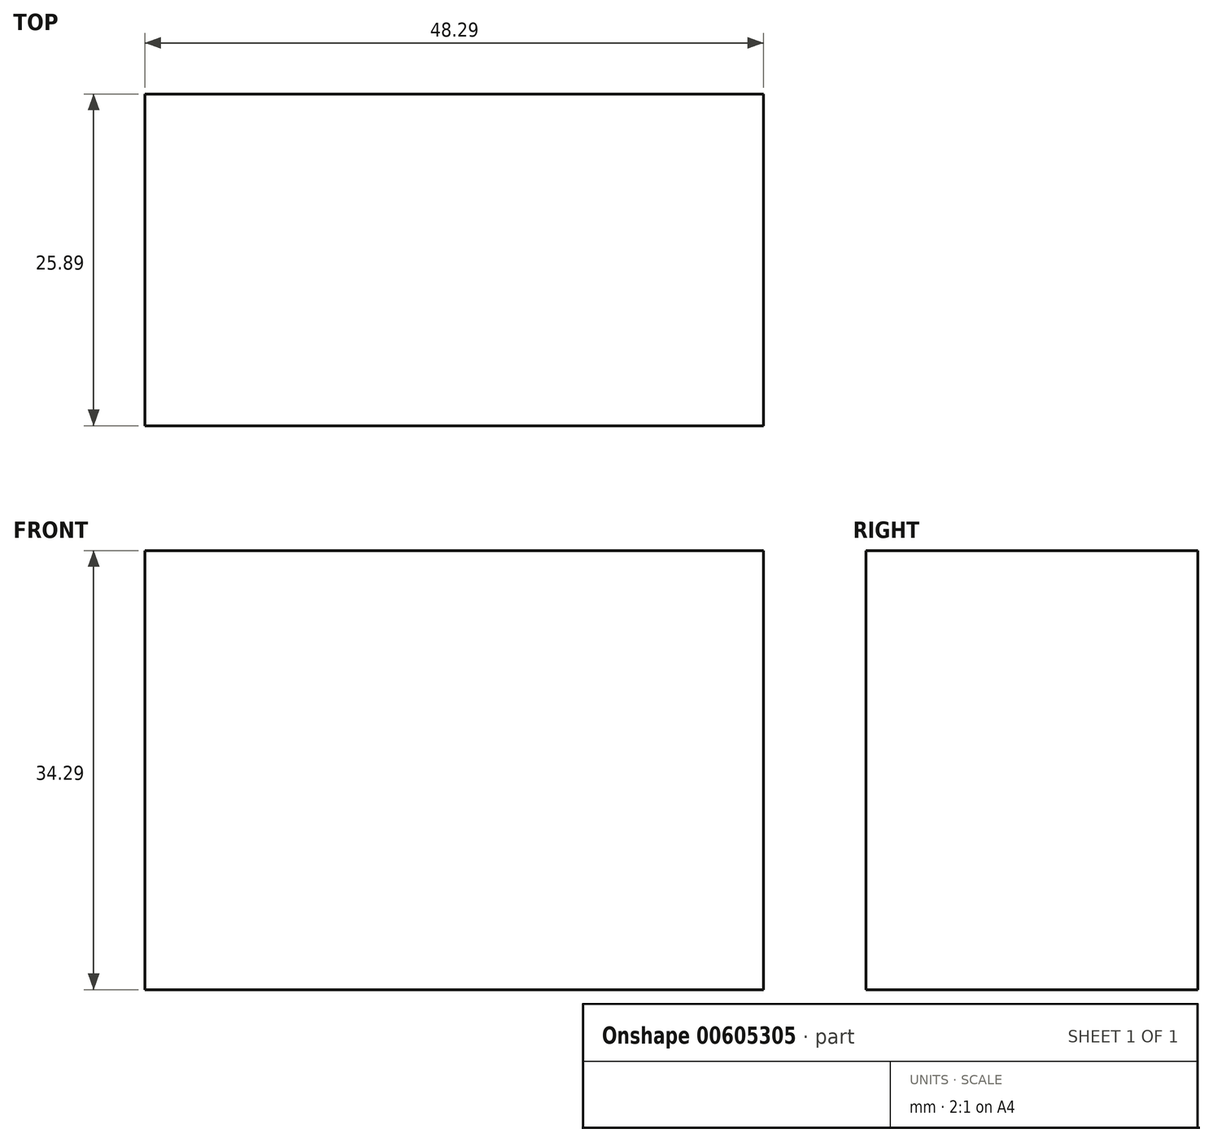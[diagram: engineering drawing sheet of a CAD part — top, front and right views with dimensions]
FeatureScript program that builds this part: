
annotation { "Feature Type Name" : "Feature", "Feature Type Description" : "" }
export const myFeature = defineFeature(function(context is Context, id is Id, definition is map)
    precondition{}
    {
        {
            var Q0;
            Q0=qCreatedBy(makeId("Top.planeOp"),FACE);
            var sketch = newSketch(context, id + "F0", { "sketchPlane" : qUnion([Q0])});
            skLineSegment(sketch, "E0.bottom", {"start": v(0, 0) * mm, "end": v(48.29, 0) * mm});
            skLineSegment(sketch, "E0.top", {"start": v(0, 25.9) * mm, "end": v(48.29, 25.9) * mm});
            skLineSegment(sketch, "E0.left", {"start": v(0, 0) * mm, "end": v(0, 25.9) * mm});
            skLineSegment(sketch, "E0.right", {"start": v(48.29, 0) * mm, "end": v(48.29, 25.9) * mm});
            skSolve(sketch);
        }
        {
            var Q0;
            Q0 = qSketchRegion(id + "F0", true);
            extrude(context, id + "F1", {"entities" : qUnion([Q0]), "depth" : 34.3 * mm, "offsetDistance" : 25.4 * mm});
        }
    });
